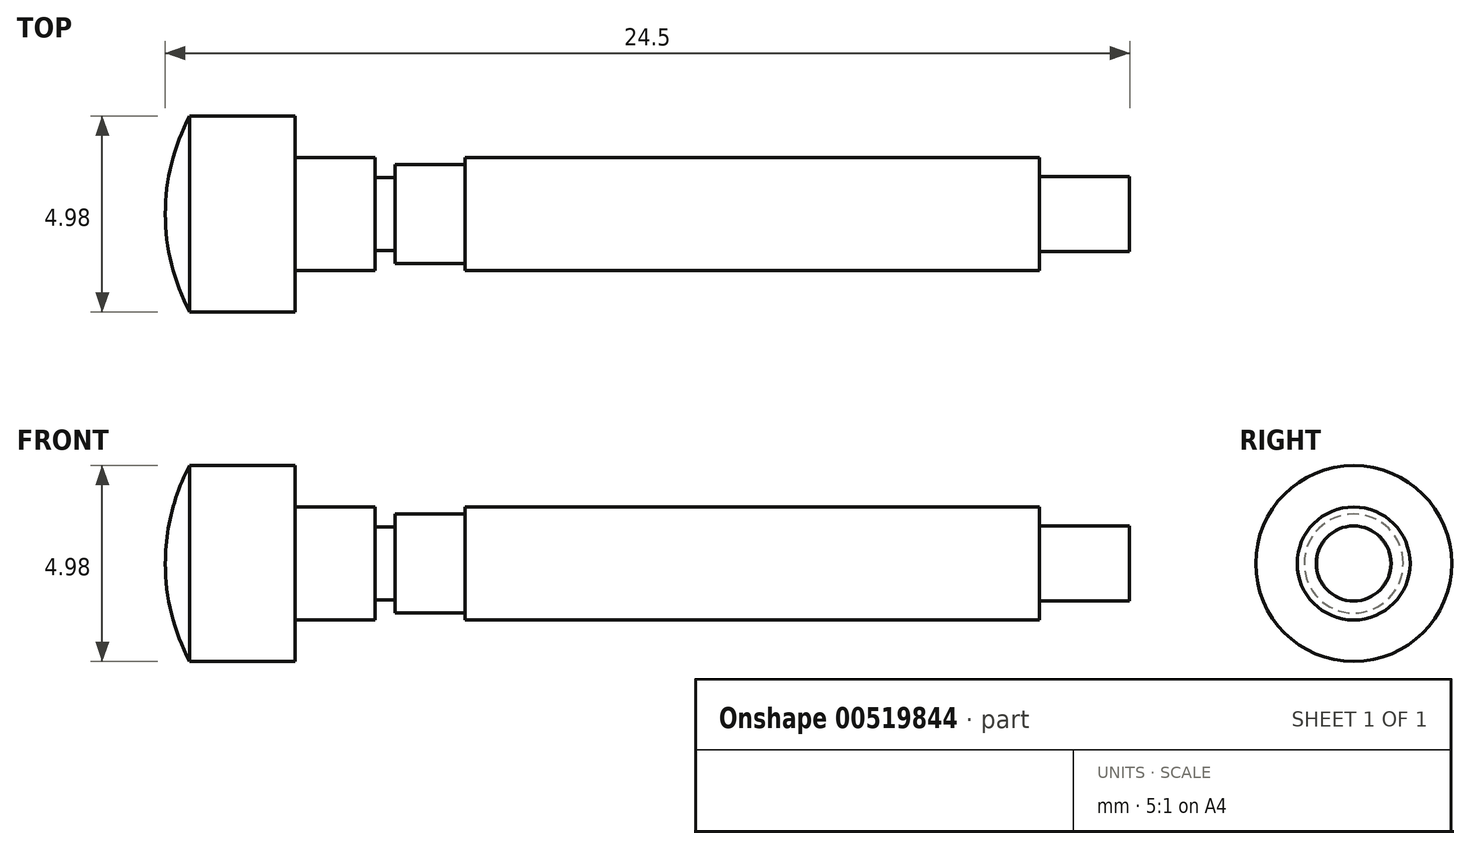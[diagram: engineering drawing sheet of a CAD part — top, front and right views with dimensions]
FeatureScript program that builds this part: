
annotation { "Feature Type Name" : "Feature", "Feature Type Description" : "" }
export const myFeature = defineFeature(function(context is Context, id is Id, definition is map)
    precondition{}
    {
        {
            var Q0;
            Q0=qCreatedBy(makeId("Front.planeOp"),FACE);
            var sketch = newSketch(context, id + "F0", { "sketchPlane" : qUnion([Q0])});
            skLineSegment(sketch, "E0", {"start": v(0.62, 2.49) * mm, "end": v(3.3, 2.49) * mm});
            skLineSegment(sketch, "E1", {"start": v(24.5, 0) * mm, "end": v(0, 0) * mm});
            skLineSegment(sketch, "E2", {"start": v(3.3, 2.49) * mm, "end": v(3.3, 1.44) * mm});
            skLineSegment(sketch, "E3", {"start": v(3.3, 1.44) * mm, "end": v(5.33, 1.44) * mm});
            skLineSegment(sketch, "E4", {"start": v(24.5, 0.95) * mm, "end": v(24.5, 0) * mm});
            skLineSegment(sketch, "E5", {"start": v(22.21, 1.44) * mm, "end": v(22.21, 0.95) * mm});
            skLineSegment(sketch, "E6", {"start": v(22.21, 0.95) * mm, "end": v(24.5, 0.95) * mm});
            skPoint(sketch, "E7.orphan", {"position": v(24.5, 1.44) * mm});
            skLineSegment(sketch, "E8", {"start": v(5.33, 1.44) * mm, "end": v(5.33, 0.93) * mm});
            skLineSegment(sketch, "E9", {"start": v(5.33, 0.93) * mm, "end": v(5.84, 0.93) * mm});
            skLineSegment(sketch, "E10", {"start": v(5.84, 0.93) * mm, "end": v(5.84, 1.26) * mm});
            skLineSegment(sketch, "E11", {"start": v(5.84, 1.26) * mm, "end": v(7.62, 1.26) * mm});
            skLineSegment(sketch, "E12", {"start": v(7.62, 1.26) * mm, "end": v(7.62, 1.44) * mm});
            skLineSegment(sketch, "E13.trimOffspring", {"start": v(7.62, 1.44) * mm, "end": v(22.21, 1.44) * mm});
            skArc(sketch, "E14", {"start": v(0.62, 2.49) * mm, "mid": v(0.16, 1.28) * mm, "end": v(0, 0) * mm});
            skPoint(sketch, "E15.orphan", {"position": v(0, 2.49) * mm});
            skSolve(sketch);
        }
        {
            var Q0;
            Q0 = qSketchRegion(id + "F0", true);
            var Q1;
            Q1=sQuery(id+"F0.wireOp",EDGE,"E1");
            revolve(context, id + "F1", {"entities" : qUnion([Q0]), "axis" : qUnion([Q1]), "revolveType" : RevolveType.FULL});
        }
    });
